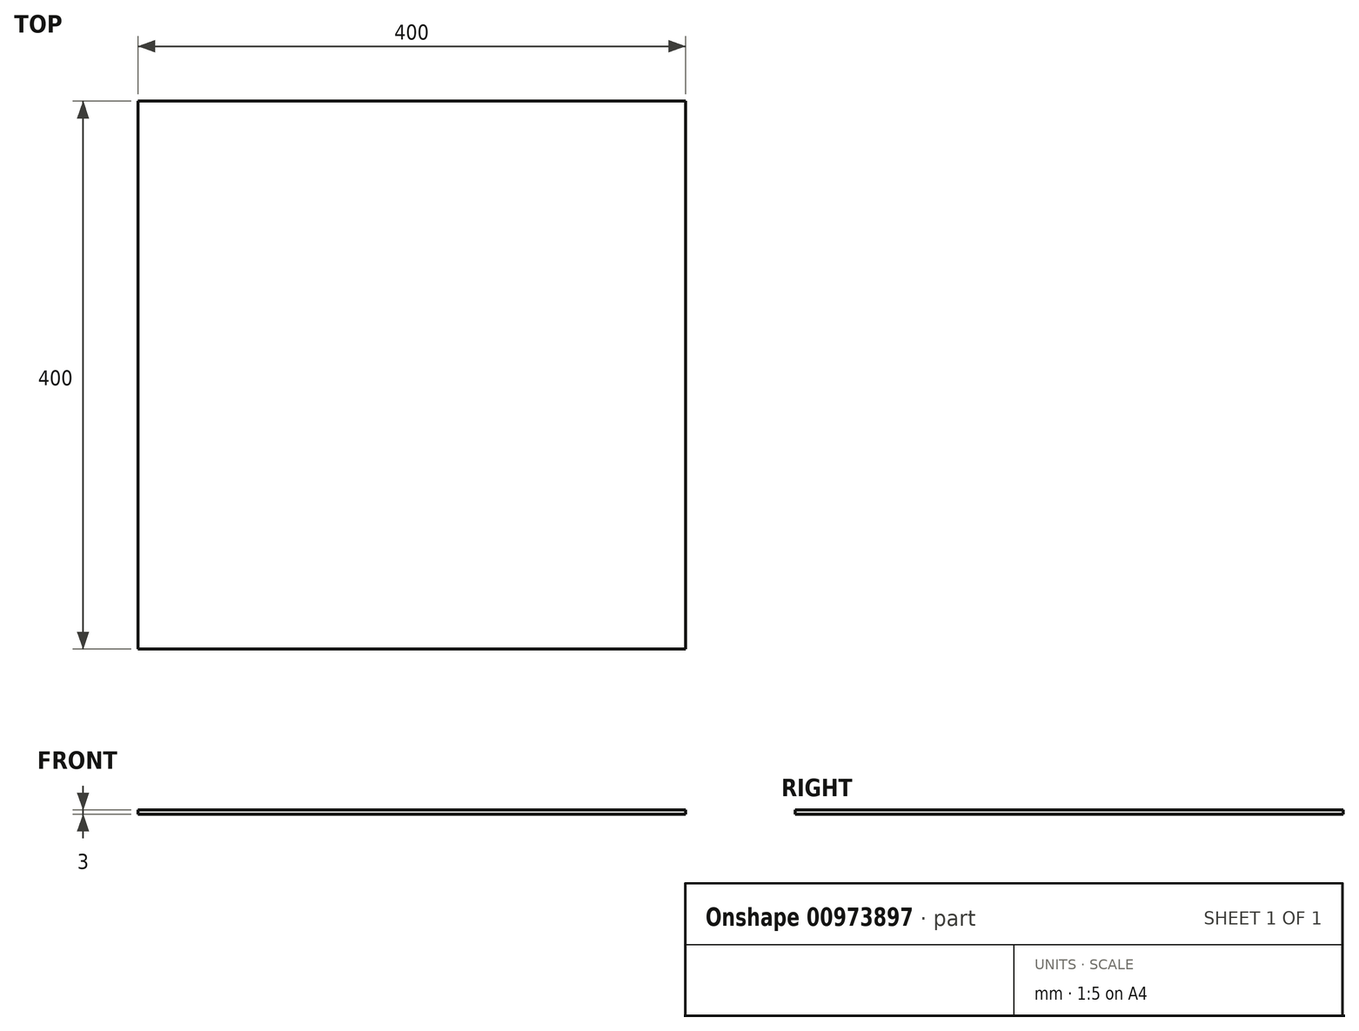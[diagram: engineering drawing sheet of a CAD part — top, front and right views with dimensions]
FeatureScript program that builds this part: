
annotation { "Feature Type Name" : "Feature", "Feature Type Description" : "" }
export const myFeature = defineFeature(function(context is Context, id is Id, definition is map)
    precondition{}
    {
        {
            var Q0;
            Q0=qCreatedBy(makeId("Top.planeOp"),FACE);
            var sketch = newSketch(context, id + "F0", { "sketchPlane" : qUnion([Q0])});
            skLineSegment(sketch, "E0.bottom", {"start": v(-200, -200) * mm, "end": v(200, -200) * mm});
            skLineSegment(sketch, "E0.top", {"start": v(-200, 200) * mm, "end": v(200, 200) * mm});
            skLineSegment(sketch, "E0.left", {"start": v(-200, -200) * mm, "end": v(-200, 200) * mm});
            skLineSegment(sketch, "E0.right", {"start": v(200, -200) * mm, "end": v(200, 200) * mm});
            skSolve(sketch);
        }
        {
            var Q0;
            Q0 = qSketchRegion(id + "F0", true);
            extrude(context, id + "F1", {"entities" : qUnion([Q0]), "depth" : 3 * mm, "offsetDistance" : 25 * mm});
        }
    });
